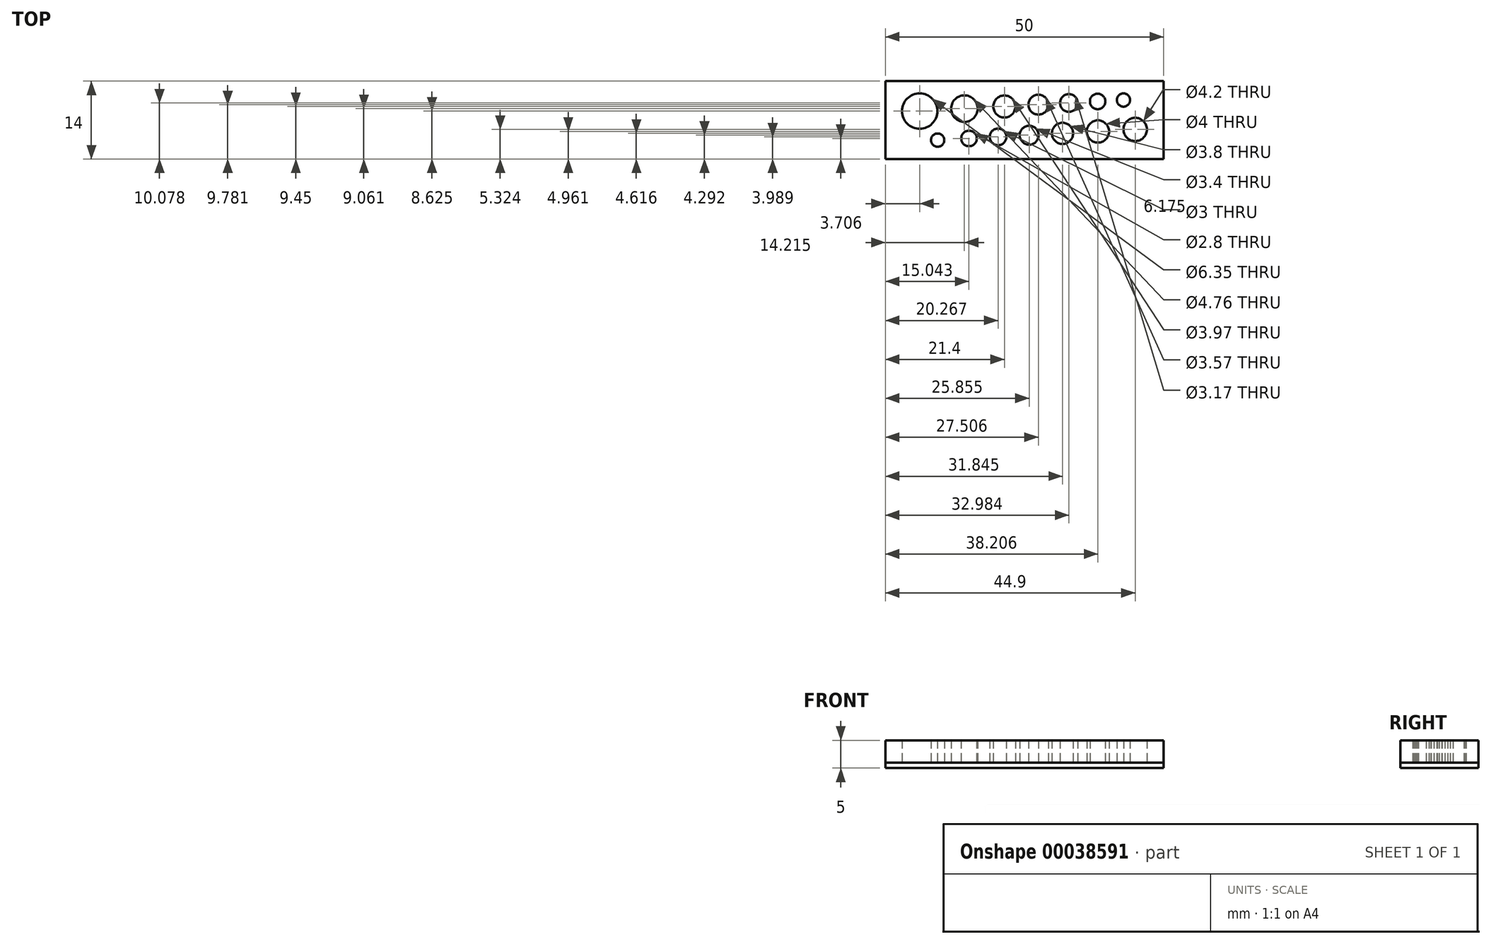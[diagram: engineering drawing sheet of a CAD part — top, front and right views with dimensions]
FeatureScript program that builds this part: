
annotation { "Feature Type Name" : "Feature", "Feature Type Description" : "" }
export const myFeature = defineFeature(function(context is Context, id is Id, definition is map)
    precondition{}
    {
        {
            var Q0;
            Q0=qCreatedBy(makeId("Top.planeOp"),FACE);
            var sketch = newSketch(context, id + "F0", { "sketchPlane" : qUnion([Q0])});
            skLineSegment(sketch, "E0.rect.bottom", {"start": v(25, 7) * mm, "end": v(-25, 7) * mm});
            skLineSegment(sketch, "E0.rect.top", {"start": v(25, -7) * mm, "end": v(-25, -7) * mm});
            skLineSegment(sketch, "E0.rect.left", {"start": v(25, 7) * mm, "end": v(25, -7) * mm});
            skLineSegment(sketch, "E0.rect.right", {"start": v(-25, 7) * mm, "end": v(-25, -7) * mm});
            skPoint(sketch, "E0.rect.middle", {"position": v(0, 0) * mm});
            skLineSegment(sketch, "E1", {"start": v(-25, 1.3) * mm, "end": v(25, 4) * mm, "construction": true});
            skLineSegment(sketch, "E2", {"start": v(-25, -4.1) * mm, "end": v(25, -1.4) * mm, "construction": true});
            skCircle(sketch, "E3", {"center": v(13.15, 3.36) * mm, "radius": 1.39 * mm});
            skCircle(sketch, "E4", {"center": v(7.98, 3.08) * mm, "radius": 1.59 * mm});
            skCircle(sketch, "E5", {"center": v(2.5, 2.78) * mm, "radius": 1.79 * mm});
            skCircle(sketch, "E6", {"center": v(-3.6, 2.45) * mm, "radius": 1.98 * mm});
            skCircle(sketch, "E7", {"center": v(-10.79, 2.06) * mm, "radius": 2.38 * mm});
            skCircle(sketch, "E8", {"center": v(-18.83, 1.62) * mm, "radius": 3.18 * mm});
            skCircle(sketch, "E9", {"center": v(17.8, 3.6) * mm, "radius": 1.2 * mm});
            skCircle(sketch, "E10", {"center": v(-9.96, -3.3) * mm, "radius": 1.4 * mm});
            skCircle(sketch, "E11", {"center": v(-4.73, -3.01) * mm, "radius": 1.5 * mm});
            skCircle(sketch, "E12", {"center": v(0.86, -2.7) * mm, "radius": 1.7 * mm});
            skCircle(sketch, "E13", {"center": v(6.84, -2.38) * mm, "radius": 1.9 * mm});
            skCircle(sketch, "E14", {"center": v(13.2, -2.04) * mm, "radius": 2 * mm});
            skCircle(sketch, "E15", {"center": v(19.9, -1.68) * mm, "radius": 2.1 * mm});
            skLineSegment(sketch, "E16", {"start": v(-23.58, 4.8) * mm, "end": v(23.45, 4.8) * mm, "construction": true});
            skLineSegment(sketch, "E17", {"start": v(23.58, -4.8) * mm, "end": v(-23.27, -4.8) * mm, "construction": true});
            skCircle(sketch, "E18", {"center": v(-15.6, -3.6) * mm, "radius": 1.2 * mm});
            skSolve(sketch);
        }
        {
            var Q0;
            Q0 = qSketchRegion(id + "F0", true);
            var Q1;
            Q1=makeQuery(id+"F0.imprint","IMPRINT",FACE,{"disambiguationData":[TD([[makeQuery(id+"F0.imprint","IMPRINT",EDGE,{"derivedFrom":sQuery(id+"F0.wireOp",EDGE,"E8")}),1.0]])]});
            var Q2;
            Q2=makeQuery(id+"F0.imprint","IMPRINT",FACE,{"disambiguationData":[TD([[makeQuery(id+"F0.imprint","IMPRINT",EDGE,{"derivedFrom":sQuery(id+"F0.wireOp",EDGE,"E7")}),1.0]])]});
            var Q3;
            Q3=makeQuery(id+"F0.imprint","IMPRINT",FACE,{"disambiguationData":[TD([[makeQuery(id+"F0.imprint","IMPRINT",EDGE,{"derivedFrom":sQuery(id+"F0.wireOp",EDGE,"E6")}),1.0]])]});
            var Q4;
            Q4=makeQuery(id+"F0.imprint","IMPRINT",FACE,{"disambiguationData":[TD([[makeQuery(id+"F0.imprint","IMPRINT",EDGE,{"derivedFrom":sQuery(id+"F0.wireOp",EDGE,"E5")}),1.0]])]});
            var Q5;
            Q5=makeQuery(id+"F0.imprint","IMPRINT",FACE,{"disambiguationData":[TD([[makeQuery(id+"F0.imprint","IMPRINT",EDGE,{"derivedFrom":sQuery(id+"F0.wireOp",EDGE,"E4")}),1.0]])]});
            var Q6;
            Q6=makeQuery(id+"F0.imprint","IMPRINT",FACE,{"disambiguationData":[TD([[makeQuery(id+"F0.imprint","IMPRINT",EDGE,{"derivedFrom":sQuery(id+"F0.wireOp",EDGE,"E3")}),1.0]])]});
            var Q7;
            Q7=makeQuery(id+"F0.imprint","IMPRINT",FACE,{"disambiguationData":[TD([[makeQuery(id+"F0.imprint","IMPRINT",EDGE,{"derivedFrom":sQuery(id+"F0.wireOp",EDGE,"E9")}),1.0]])]});
            var Q8;
            Q8=makeQuery(id+"F0.imprint","IMPRINT",FACE,{"disambiguationData":[TD([[makeQuery(id+"F0.imprint","IMPRINT",EDGE,{"derivedFrom":sQuery(id+"F0.wireOp",EDGE,"E18")}),1.0]])]});
            var Q9;
            Q9=makeQuery(id+"F0.imprint","IMPRINT",FACE,{"disambiguationData":[TD([[makeQuery(id+"F0.imprint","IMPRINT",EDGE,{"derivedFrom":sQuery(id+"F0.wireOp",EDGE,"E10")}),1.0]])]});
            var Q10;
            Q10=makeQuery(id+"F0.imprint","IMPRINT",FACE,{"disambiguationData":[TD([[makeQuery(id+"F0.imprint","IMPRINT",EDGE,{"derivedFrom":sQuery(id+"F0.wireOp",EDGE,"E11")}),1.0]])]});
            var Q11;
            Q11=makeQuery(id+"F0.imprint","IMPRINT",FACE,{"disambiguationData":[TD([[makeQuery(id+"F0.imprint","IMPRINT",EDGE,{"derivedFrom":sQuery(id+"F0.wireOp",EDGE,"E12")}),1.0]])]});
            var Q12;
            Q12=makeQuery(id+"F0.imprint","IMPRINT",FACE,{"disambiguationData":[TD([[makeQuery(id+"F0.imprint","IMPRINT",EDGE,{"derivedFrom":sQuery(id+"F0.wireOp",EDGE,"E13")}),1.0]])]});
            var Q13;
            Q13=makeQuery(id+"F0.imprint","IMPRINT",FACE,{"disambiguationData":[TD([[makeQuery(id+"F0.imprint","IMPRINT",EDGE,{"derivedFrom":sQuery(id+"F0.wireOp",EDGE,"E14")}),1.0]])]});
            var Q14;
            Q14=makeQuery(id+"F0.imprint","IMPRINT",FACE,{"disambiguationData":[TD([[makeQuery(id+"F0.imprint","IMPRINT",EDGE,{"derivedFrom":sQuery(id+"F0.wireOp",EDGE,"E15")}),1.0]])]});
            extrude(context, id + "F1", {"entities" : qUnion([Q0, Q1, Q2, Q3, Q4, Q5, Q6, Q7, Q8, Q9, Q10, Q11, Q12, Q13, Q14]), "oppositeDirection" : true, "depth" : 1 * mm});
        }
        {
            var Q0;
            Q0 = qSketchRegion(id + "F0", true);
            extrude(context, id + "F2", {"entities" : qUnion([Q0]), "depth" : 4 * mm});
        }
    });
